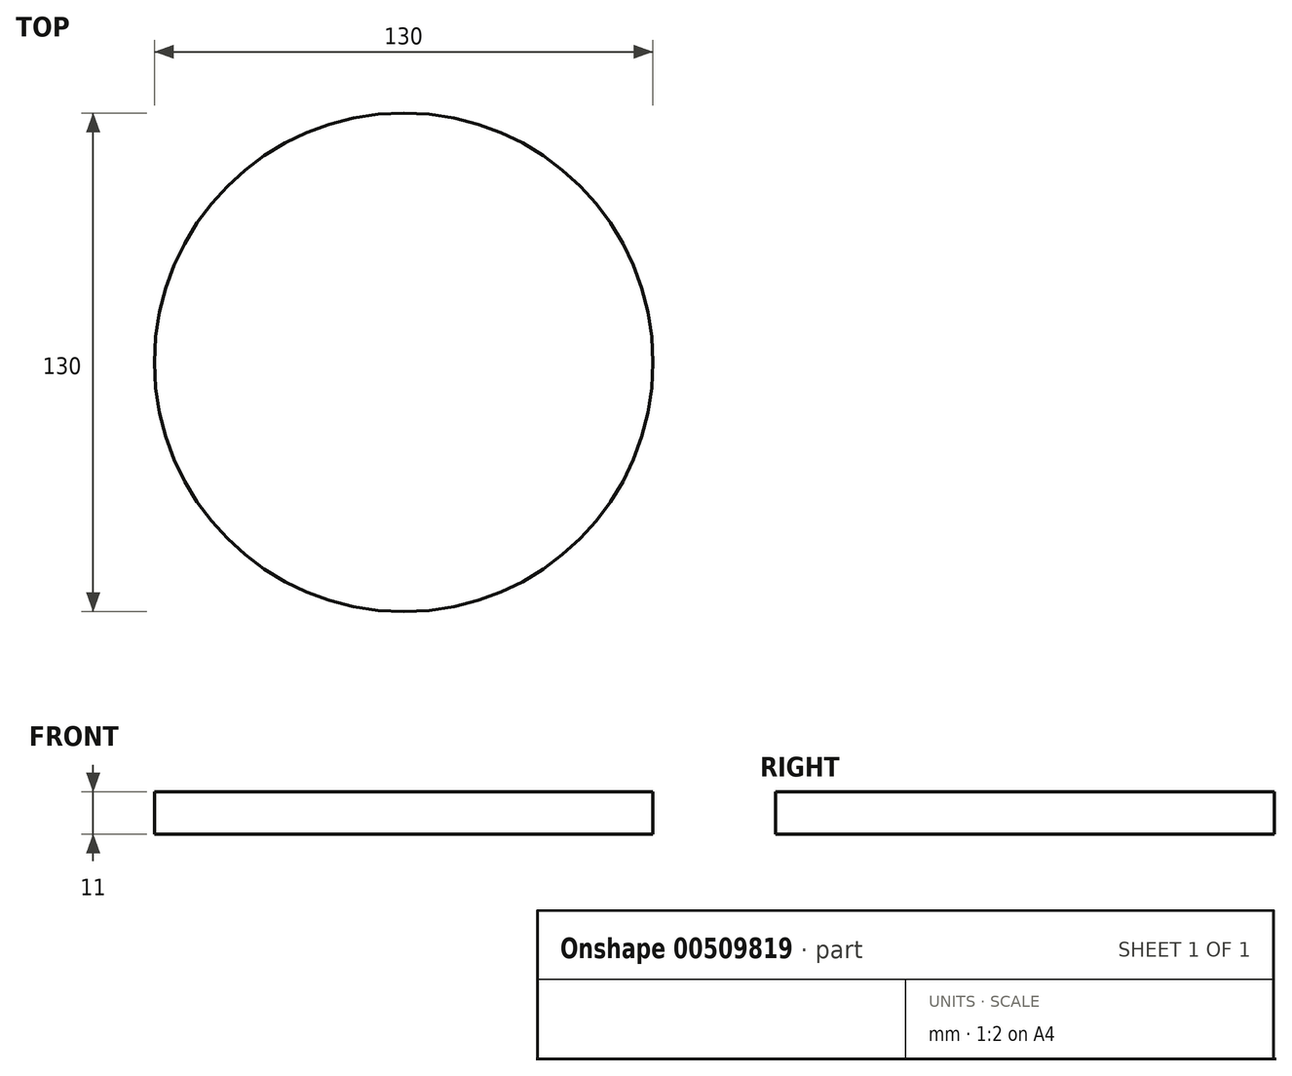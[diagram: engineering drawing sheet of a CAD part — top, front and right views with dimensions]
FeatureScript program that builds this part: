
annotation { "Feature Type Name" : "Feature", "Feature Type Description" : "" }
export const myFeature = defineFeature(function(context is Context, id is Id, definition is map)
    precondition{}
    {
        {
            var Q0;
            Q0=qCreatedBy(makeId("Front.planeOp"),FACE);
            var sketch = newSketch(context, id + "F0", { "sketchPlane" : qUnion([Q0])});
            skLineSegment(sketch, "E0", {"start": v(65, 5.5) * mm, "end": v(0, 5.5) * mm});
            skLineSegment(sketch, "E1", {"start": v(0, 5.5) * mm, "end": v(0, 0) * mm});
            skLineSegment(sketch, "E2", {"start": v(0, 0) * mm, "end": v(0, -5.5) * mm});
            skLineSegment(sketch, "E3", {"start": v(0, -5.5) * mm, "end": v(65, -5.5) * mm});
            skLineSegment(sketch, "E4", {"start": v(65, 5.5) * mm, "end": v(65, -5.5) * mm});
            skSolve(sketch);
        }
        {
            var Q0;
            Q0 = qSketchRegion(id + "F0", true);
            var Q1;
            Q1=sQuery(id+"F0.wireOp",EDGE,"E2");
            revolve(context, id + "F1", {"surfaceOperationType" : NewSurfaceOperationType.NEW, "entities" : qUnion([Q0]), "axis" : qUnion([Q1]), "revolveType" : RevolveType.FULL});
        }
    });
